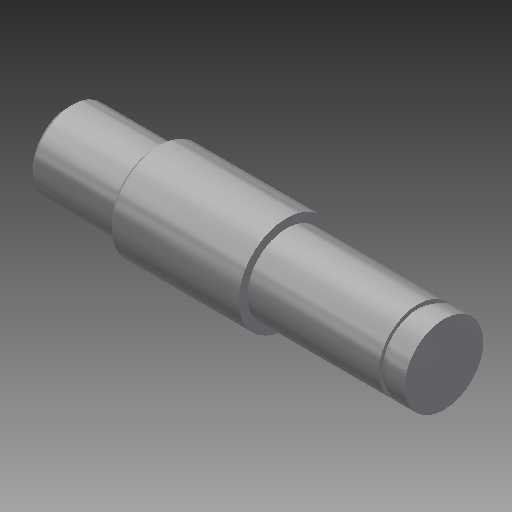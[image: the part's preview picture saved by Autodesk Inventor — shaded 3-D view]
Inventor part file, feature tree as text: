
AUTODESK INVENTOR PART (.ipt)
format: ipt  version: 2019 (Build 230136000, 136)  size: 148,480 bytes
history: native  units: mm
features: other x6, chamfer x2
ambient origin geometry x6: Origin, XZ Plane, XY Plane, X Axis, Y Axis, Z Axis
bodies: Body1 (feature_tree)
feature tree (8):
  other  "實體1"
  other  "迴轉1"
  other  "扣環槽3"
  chamfer  "倒角2"  [1 undecoded]
  chamfer  "倒角1"  Distance=9.0mm
  other  "起始平面"
  other  "主要草圖"
  other  "iFeature27:3"
note: 1 required parameter value undecoded (feature->parameter linkage not recoverable at this tier; creation-order binding heuristic only, values carry confidence <= 0.55)
